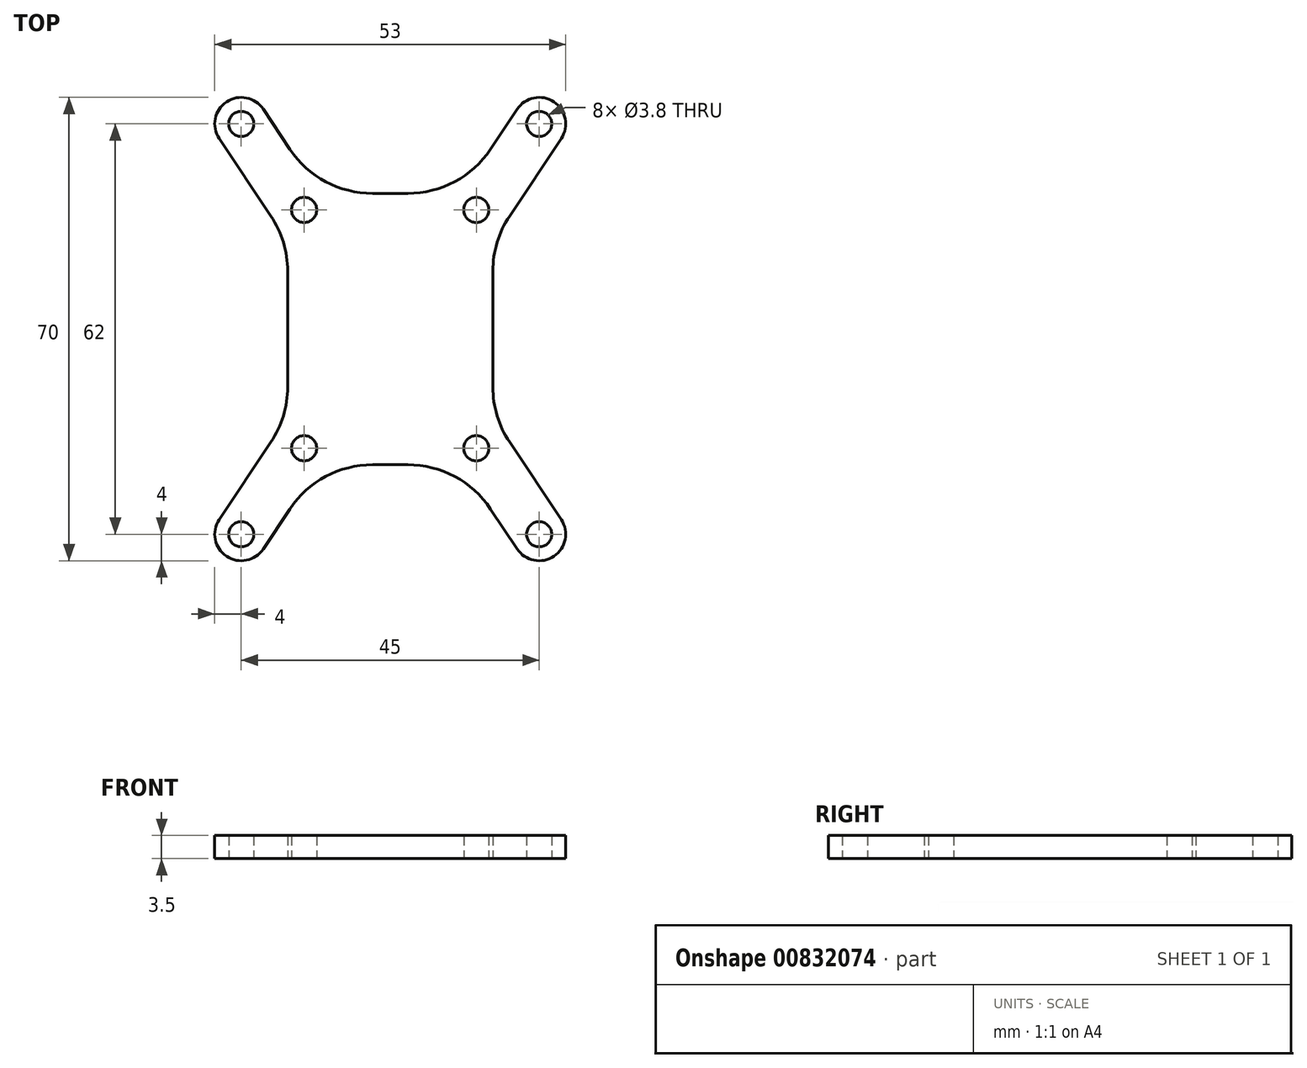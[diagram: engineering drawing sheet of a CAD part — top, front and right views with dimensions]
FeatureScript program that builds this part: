
annotation { "Feature Type Name" : "Feature", "Feature Type Description" : "" }
export const myFeature = defineFeature(function(context is Context, id is Id, definition is map)
    precondition{}
    {
        {
            var Q0;
            Q0=qCreatedBy(makeId("Top.planeOp"),FACE);
            var sketch = newSketch(context, id + "F0", { "sketchPlane" : qUnion([Q0])});
            skLineSegment(sketch, "E0", {"start": v(-19.17, 33.22) * mm, "end": v(-15.15, 27.18) * mm});
            skLineSegment(sketch, "E1", {"start": v(-2.66, 20.5) * mm, "end": v(2.66, 20.5) * mm});
            skLineSegment(sketch, "E2", {"start": v(15.15, 27.18) * mm, "end": v(19.17, 33.22) * mm});
            skLineSegment(sketch, "E3", {"start": v(-25.83, 28.78) * mm, "end": v(-18.02, 17.07) * mm});
            skLineSegment(sketch, "E4", {"start": v(-15.5, 8.75) * mm, "end": v(-15.5, -8.75) * mm});
            skLineSegment(sketch, "E5", {"start": v(-18.02, -17.07) * mm, "end": v(-25.83, -28.78) * mm});
            skLineSegment(sketch, "E6", {"start": v(-19.17, -33.22) * mm, "end": v(-15.15, -27.18) * mm});
            skLineSegment(sketch, "E7", {"start": v(-2.66, -20.5) * mm, "end": v(2.66, -20.5) * mm});
            skLineSegment(sketch, "E8", {"start": v(15.15, -27.18) * mm, "end": v(19.17, -33.22) * mm});
            skLineSegment(sketch, "E9", {"start": v(25.83, -28.78) * mm, "end": v(18.02, -17.07) * mm});
            skLineSegment(sketch, "E10", {"start": v(15.5, -8.75) * mm, "end": v(15.5, 8.75) * mm});
            skLineSegment(sketch, "E11", {"start": v(18.02, 17.07) * mm, "end": v(25.83, 28.78) * mm});
            skLineSegment(sketch, "E12.bottom", {"start": v(-15.5, 20.5) * mm, "end": v(15.5, 20.5) * mm, "construction": true});
            skLineSegment(sketch, "E12.top", {"start": v(-15.5, -20.5) * mm, "end": v(15.5, -20.5) * mm, "construction": true});
            skLineSegment(sketch, "E12.left", {"start": v(-15.5, 20.5) * mm, "end": v(-15.5, -20.5) * mm, "construction": true});
            skLineSegment(sketch, "E12.right", {"start": v(15.5, 20.5) * mm, "end": v(15.5, -20.5) * mm, "construction": true});
            skArc(sketch, "E13", {"start": v(-19.17, 33.22) * mm, "mid": v(-24.72, 34.33) * mm, "end": v(-25.83, 28.78) * mm});
            skArc(sketch, "E14", {"start": v(25.83, 28.78) * mm, "mid": v(24.72, 34.33) * mm, "end": v(19.17, 33.22) * mm});
            skArc(sketch, "E15", {"start": v(19.17, -33.22) * mm, "mid": v(24.72, -34.33) * mm, "end": v(25.83, -28.78) * mm});
            skArc(sketch, "E16", {"start": v(-25.83, -28.78) * mm, "mid": v(-24.72, -34.33) * mm, "end": v(-19.17, -33.22) * mm});
            skCircle(sketch, "E17", {"center": v(-22.5, 31) * mm, "radius": 1.9 * mm});
            skCircle(sketch, "E18", {"center": v(22.5, 31) * mm, "radius": 1.9 * mm});
            skCircle(sketch, "E19", {"center": v(22.5, -31) * mm, "radius": 1.9 * mm});
            skCircle(sketch, "E20", {"center": v(-22.5, -31) * mm, "radius": 1.9 * mm});
            skLineSegment(sketch, "E21", {"start": v(-15.5, 20.5) * mm, "end": v(15.5, -20.5) * mm, "construction": true});
            skLineSegment(sketch, "E22", {"start": v(-22.5, 31) * mm, "end": v(-15.5, 20.5) * mm, "construction": true});
            skLineSegment(sketch, "E23", {"start": v(-15.5, -20.5) * mm, "end": v(-22.5, -31) * mm, "construction": true});
            skPoint(sketch, "E24.visualSharp", {"position": v(-15.5, 13.29) * mm});
            skArc(sketch, "E24.filletArc", {"start": v(-15.5, 8.75) * mm, "mid": v(-16.14, 13.1) * mm, "end": v(-18.02, 17.07) * mm});
            skPoint(sketch, "E25.visualSharp", {"position": v(-15.5, -13.29) * mm});
            skArc(sketch, "E25.filletArc", {"start": v(-18.02, -17.07) * mm, "mid": v(-16.14, -13.1) * mm, "end": v(-15.5, -8.75) * mm});
            skPoint(sketch, "E26.visualSharp", {"position": v(10.7, -20.5) * mm});
            skArc(sketch, "E26.filletArc", {"start": v(15.15, -27.18) * mm, "mid": v(9.74, -22.27) * mm, "end": v(2.66, -20.5) * mm});
            skPoint(sketch, "E27.visualSharp", {"position": v(-10.7, -20.5) * mm});
            skArc(sketch, "E27.filletArc", {"start": v(-2.66, -20.5) * mm, "mid": v(-9.74, -22.27) * mm, "end": v(-15.15, -27.18) * mm});
            skPoint(sketch, "E28.visualSharp", {"position": v(15.5, -13.29) * mm});
            skArc(sketch, "E28.filletArc", {"start": v(15.5, -8.75) * mm, "mid": v(16.14, -13.1) * mm, "end": v(18.02, -17.07) * mm});
            skPoint(sketch, "E29.visualSharp", {"position": v(15.5, 13.29) * mm});
            skArc(sketch, "E29.filletArc", {"start": v(18.02, 17.07) * mm, "mid": v(16.14, 13.1) * mm, "end": v(15.5, 8.75) * mm});
            skPoint(sketch, "E30.visualSharp", {"position": v(10.7, 20.5) * mm});
            skArc(sketch, "E30.filletArc", {"start": v(2.66, 20.5) * mm, "mid": v(9.74, 22.27) * mm, "end": v(15.15, 27.18) * mm});
            skPoint(sketch, "E31.visualSharp", {"position": v(-10.7, 20.5) * mm});
            skArc(sketch, "E31.filletArc", {"start": v(-15.15, 27.18) * mm, "mid": v(-9.74, 22.27) * mm, "end": v(-2.66, 20.5) * mm});
            skCircle(sketch, "E32", {"center": v(13, 18) * mm, "radius": 1.9 * mm});
            skCircle(sketch, "E33", {"center": v(13, -18) * mm, "radius": 1.9 * mm});
            skCircle(sketch, "E34", {"center": v(-13, -18) * mm, "radius": 1.9 * mm});
            skCircle(sketch, "E35", {"center": v(-13, 18) * mm, "radius": 1.9 * mm});
            skSolve(sketch);
        }
        {
            var Q0;
            Q0 = qSketchRegion(id + "F0", true);
            extrude(context, id + "F1", {"entities" : qUnion([Q0]), "depth" : 3.5 * mm, "offsetDistance" : 25 * mm});
        }
    });
